FCSTD DOCUMENT  (FreeCAD 1.0R39109 (Git))
Label: asm_cam_holder
License: All rights reserved
LicenseURL: https://en.wikipedia.org/wiki/All_rights_reserved
objects: App::Link×24, App::FeaturePython×5, Assembly::AssemblyLink×4, Assembly::JointGroup×1, Assembly::AssemblyObject×1
EXTERNAL_REF file=../parts/cam_holder/cam_holder_plate.FCStd obj=Body
EXTERNAL_REF file=asm_shf.FCStd obj=Assembly
EXTERNAL_REF file=asm_shf.FCStd obj=SHF12
EXTERNAL_REF file=asm_shf.FCStd obj=Hex_socket_head_cap_screw_DIN_912_M4_15_0
EXTERNAL_REF file=asm_shf.FCStd obj=Hex_socket_head_cap_screw_DIN_912_M5_15_0
EXTERNAL_REF file=asm_shf.FCStd obj=Hex_socket_head_cap_screw_DIN_912_M5_15_001
EXTERNAL_REF file=asm_rpi.FCStd obj=Assembly
EXTERNAL_REF file=asm_rpi.FCStd obj=Raspberry_Pi_4_Model_B
EXTERNAL_REF file=asm_rpi.FCStd obj=Hex_screw_M2_5_04_0
EXTERNAL_REF file=asm_rpi.FCStd obj=Hex_screw_M2_5_04_001
EXTERNAL_REF file=asm_rpi.FCStd obj=Hex_screw_M2_5_04_002
EXTERNAL_REF file=asm_rpi.FCStd obj=Hex_screw_M2_5_04_003
EXTERNAL_REF file=asm_cam_mount.FCStd obj=Assembly
EXTERNAL_REF file=asm_cam_mount.FCStd obj=cam_holder_base
EXTERNAL_REF file=asm_cam_mount.FCStd obj=Raspberry_Pi_HQ_Camera_with_cs_mount_lens_v014
EXTERNAL_REF file=asm_cam_mount.FCStd obj=Hex_screw_M2_5_04_0
EXTERNAL_REF file=asm_cam_mount.FCStd obj=Hex_screw_M2_5_04_001
EXTERNAL_REF file=asm_cam_mount.FCStd obj=Hex_screw_M2_5_04_002
EXTERNAL_REF file=asm_cam_mount.FCStd obj=Hex_screw_M2_5_04_003
EXTERNAL_REF file=asm_cam_mount.FCStd obj=Hex_screw_M4_10_0
EXTERNAL_REF file=asm_cam_mount.FCStd obj=Hex_screw_M4_10_001
EXTERNAL_REF file=asm_cam_mount.FCStd obj=Hex_screw_M4_10_002
EXTERNAL_REF file=asm_cam_mount.FCStd obj=Hex_screw_M4_10_003

FEATURE [App::Link] cam_holder_plate
  LinkedObject = -> <external ../parts/cam_holder/cam_holder_plate.FCStd>#Body
FEATURE [App::FeaturePython] GroundedJoint  # Assembly grounded joint (typed FeaturePython)
  ObjectToGround = -> cam_holder_plate
FEATURE [App::Link] SHF12
  LinkedObject = -> <external asm_shf.FCStd>#SHF12
FEATURE [App::Link] Hex_socket_head_cap_screw_DIN_912_M4_15_0  label="Hex socket head cap screw DIN 912 M4 15.0"
  LinkPlacement = pos=(12.25,6.5,11.5) rot=(0,-1,0;1.5708rad)
  LinkedObject = -> <external asm_shf.FCStd>#Hex_socket_head_cap_screw_DIN_912_M4_15_0
  Placement = pos=(12.25,6.5,11.5) rot=(0,-1,0;1.5708rad)
FEATURE [App::Link] Hex_socket_head_cap_screw_DIN_912_M5_15_0  label="Hex socket head cap screw DIN 912 M5 15.0"
  LinkPlacement = pos=(18,11,1.16e-14) rot=(0.57735,-0.57735,0.57735;2.0944rad)
  LinkedObject = -> <external asm_shf.FCStd>#Hex_socket_head_cap_screw_DIN_912_M5_15_0
  Placement = pos=(18,11,1.16e-14) rot=(0.57735,-0.57735,0.57735;2.0944rad)
FEATURE [App::Link] Hex_socket_head_cap_screw_DIN_912_M5_15_001  label="Hex socket head cap screw DIN 912 M5 15.001"
  LinkPlacement = pos=(-18,11,1.16e-14) rot=(0.57735,-0.57735,0.57735;2.0944rad)
  LinkedObject = -> <external asm_shf.FCStd>#Hex_socket_head_cap_screw_DIN_912_M5_15_001
  Placement = pos=(-18,11,1.16e-14) rot=(0.57735,-0.57735,0.57735;2.0944rad)
FEATURE [Assembly::AssemblyLink] asm_SHF
  Group = -> [SHF12,Hex_socket_head_cap_screw_DIN_912_M4_15_0,Hex_socket_head_cap_screw_DIN_912_M5_15_0,Hex_socket_head_cap_screw_DIN_912_M5_15_001]
  LinkedObject = -> <external asm_shf.FCStd>#Assembly
  Origin = -> Origin001
  Placement = pos=(0,38,3) rot=(0,0.707107,0.707107;3.14159rad)
  Rigid = true
FEATURE [App::Link] SHF013
  LinkedObject = -> <external asm_shf.FCStd>#SHF12
FEATURE [App::Link] Hex_socket_head_cap_screw_DIN_912_M4_15_001  label="Hex socket head cap screw DIN 912 M4 15.001"
  LinkPlacement = pos=(12.25,6.5,11.5) rot=(0,-1,0;1.5708rad)
  LinkedObject = -> <external asm_shf.FCStd>#Hex_socket_head_cap_screw_DIN_912_M4_15_0
  Placement = pos=(12.25,6.5,11.5) rot=(0,-1,0;1.5708rad)
FEATURE [App::Link] Hex_socket_head_cap_screw_DIN_912_M5_15_002  label="Hex socket head cap screw DIN 912 M5 15.002"
  LinkPlacement = pos=(18,11,1.16e-14) rot=(0.57735,-0.57735,0.57735;2.0944rad)
  LinkedObject = -> <external asm_shf.FCStd>#Hex_socket_head_cap_screw_DIN_912_M5_15_0
  Placement = pos=(18,11,1.16e-14) rot=(0.57735,-0.57735,0.57735;2.0944rad)
FEATURE [App::Link] Hex_socket_head_cap_screw_DIN_912_M5_15_003  label="Hex socket head cap screw DIN 912 M5 15.003"
  LinkPlacement = pos=(-18,11,1.16e-14) rot=(0.57735,-0.57735,0.57735;2.0944rad)
  LinkedObject = -> <external asm_shf.FCStd>#Hex_socket_head_cap_screw_DIN_912_M5_15_001
  Placement = pos=(-18,11,1.16e-14) rot=(0.57735,-0.57735,0.57735;2.0944rad)
FEATURE [Assembly::AssemblyLink] asm_SHF001
  Group = -> [SHF013,Hex_socket_head_cap_screw_DIN_912_M4_15_001,Hex_socket_head_cap_screw_DIN_912_M5_15_002,Hex_socket_head_cap_screw_DIN_912_M5_15_003]
  LinkedObject = -> <external asm_shf.FCStd>#Assembly
  Origin = -> Origin002
  Placement = pos=(0,-38,3) rot=(1,0,0;1.5708rad)
  Rigid = true
FEATURE [App::Link] Raspberry_Pi_4_Model_B  label="Raspberry Pi 4 Model B"
  LinkPlacement = pos=(0,8.25,-5.85) rot=(1,0,0;1.5708rad)
  LinkedObject = -> <external asm_rpi.FCStd>#Raspberry_Pi_4_Model_B
  Placement = pos=(0,8.25,-5.85) rot=(1,0,0;1.5708rad)
FEATURE [App::Link] Hex_screw_M2_5_04_0  label="Hex screw M2.5 04.0"
  LinkPlacement = pos=(54.5575,25.7632,-2.56) rot=(-0.707107,0.707107,0;3.14159rad)
  LinkedObject = -> <external asm_rpi.FCStd>#Hex_screw_M2_5_04_0
  Placement = pos=(54.5575,25.7632,-2.56) rot=(-0.707107,0.707107,0;3.14159rad)
FEATURE [App::Link] Hex_screw_M2_5_04_001  label="Hex screw M2.5 04.001"
  LinkPlacement = pos=(-3.44249,-23.2368,-2.56001) rot=(-0.707107,0.707107,0;3.14159rad)
  LinkedObject = -> <external asm_rpi.FCStd>#Hex_screw_M2_5_04_001
  Placement = pos=(-3.44249,-23.2368,-2.56001) rot=(-0.707107,0.707107,0;3.14159rad)
FEATURE [App::Link] Hex_screw_M2_5_04_002  label="Hex screw M2.5 04.002"
  LinkPlacement = pos=(-3.44249,25.7632,-2.56) rot=(-0.707107,0.707107,0;3.14159rad)
  LinkedObject = -> <external asm_rpi.FCStd>#Hex_screw_M2_5_04_002
  Placement = pos=(-3.44249,25.7632,-2.56) rot=(-0.707107,0.707107,0;3.14159rad)
FEATURE [App::Link] Hex_screw_M2_5_04_003  label="Hex screw M2.5 04.003"
  LinkPlacement = pos=(54.5575,-23.2368,-2.56001) rot=(-0.707107,0.707107,0;3.14159rad)
  LinkedObject = -> <external asm_rpi.FCStd>#Hex_screw_M2_5_04_003
  Placement = pos=(54.5575,-23.2368,-2.56001) rot=(-0.707107,0.707107,0;3.14159rad)
FEATURE [Assembly::AssemblyLink] asm_rpi
  Group = -> [Raspberry_Pi_4_Model_B,Hex_screw_M2_5_04_0,Hex_screw_M2_5_04_001,Hex_screw_M2_5_04_002,Hex_screw_M2_5_04_003]
  LinkedObject = -> <external asm_rpi.FCStd>#Assembly
  Origin = -> Origin003
  Placement = pos=(-63.8,10.25,9.64) rot=(0,0,1;3.14159rad)
  Rigid = true
FEATURE [App::Link] cam_holder_base
  LinkPlacement = pos=(0,0,0) rot=(1,0,0;3.14159rad)
  LinkedObject = -> <external asm_cam_mount.FCStd>#cam_holder_base
  Placement = pos=(0,0,0) rot=(1,0,0;3.14159rad)
FEATURE [App::Link] Raspberry_Pi_HQ_Camera_with_cs_mount_lens_v014  label="Raspberry Pi HQ Camera with cs mount lens v014"
  LinkPlacement = pos=(-18.96,19,-3.8) rot=(1,0,0;1.5708rad)
  LinkedObject = -> <external asm_cam_mount.FCStd>#Raspberry_Pi_HQ_Camera_with_cs_mount_lens_v014
  Placement = pos=(-18.96,19,-3.8) rot=(1,0,0;1.5708rad)
FEATURE [App::Link] Hex_screw_M2_5_04_004  label="Hex screw M2.5 04.004"
  LinkPlacement = pos=(-7.97317,-20.5575,-6.3) rot=(0,0,1;0rad)
  LinkedObject = -> <external asm_cam_mount.FCStd>#Hex_screw_M2_5_04_0
  Placement = pos=(-7.97317,-20.5575,-6.3) rot=(0,0,1;0rad)
FEATURE [App::Link] Hex_screw_M2_5_04_005  label="Hex screw M2.5 04.005"
  LinkPlacement = pos=(22.0268,-20.5575,-6.3) rot=(0,0,1;0rad)
  LinkedObject = -> <external asm_cam_mount.FCStd>#Hex_screw_M2_5_04_001
  Placement = pos=(22.0268,-20.5575,-6.3) rot=(0,0,1;0rad)
FEATURE [App::Link] Hex_screw_M2_5_04_006  label="Hex screw M2.5 04.006"
  LinkPlacement = pos=(22.0268,-50.5575,-6.3) rot=(0,0,1;0rad)
  LinkedObject = -> <external asm_cam_mount.FCStd>#Hex_screw_M2_5_04_002
  Placement = pos=(22.0268,-50.5575,-6.3) rot=(0,0,1;0rad)
FEATURE [App::Link] Hex_screw_M2_5_04_007  label="Hex screw M2.5 04.007"
  LinkPlacement = pos=(-7.97317,-50.5575,-6.3) rot=(0,0,1;0rad)
  LinkedObject = -> <external asm_cam_mount.FCStd>#Hex_screw_M2_5_04_003
  Placement = pos=(-7.97317,-50.5575,-6.3) rot=(0,0,1;0rad)
FEATURE [App::Link] Hex_screw_M4_10_0  label="Hex screw M4 10.0"
  LinkPlacement = pos=(-25.9732,-58.0575,-20.5) rot=(0,0,1;0rad)
  LinkedObject = -> <external asm_cam_mount.FCStd>#Hex_screw_M4_10_0
  Placement = pos=(-25.9732,-58.0575,-20.5) rot=(0,0,1;0rad)
FEATURE [App::Link] Hex_screw_M4_10_001  label="Hex screw M4 10.001"
  LinkPlacement = pos=(-25.9732,-20.0575,-20.5) rot=(0,0,1;0rad)
  LinkedObject = -> <external asm_cam_mount.FCStd>#Hex_screw_M4_10_001
  Placement = pos=(-25.9732,-20.0575,-20.5) rot=(0,0,1;0rad)
FEATURE [App::Link] Hex_screw_M4_10_002  label="Hex screw M4 10.002"
  LinkPlacement = pos=(39.9468,-58.0575,-20.5) rot=(0,0,1;0rad)
  LinkedObject = -> <external asm_cam_mount.FCStd>#Hex_screw_M4_10_002
  Placement = pos=(39.9468,-58.0575,-20.5) rot=(0,0,1;0rad)
FEATURE [App::Link] Hex_screw_M4_10_003  label="Hex screw M4 10.003"
  LinkPlacement = pos=(39.9468,-20.0575,-20.5) rot=(0,0,1;0rad)
  LinkedObject = -> <external asm_cam_mount.FCStd>#Hex_screw_M4_10_003
  Placement = pos=(39.9468,-20.0575,-20.5) rot=(0,0,1;0rad)
FEATURE [Assembly::AssemblyLink] asm_cam_mount
  Group = -> [cam_holder_base,Raspberry_Pi_HQ_Camera_with_cs_mount_lens_v014,Hex_screw_M2_5_04_004,Hex_screw_M2_5_04_005,Hex_screw_M2_5_04_006,Hex_screw_M2_5_04_007,Hex_screw_M4_10_0,Hex_screw_M4_10_001,Hex_screw_M4_10_002,Hex_screw_M4_10_003]
  LinkedObject = -> <external asm_cam_mount.FCStd>#Assembly
  Origin = -> Origin004
  Placement = pos=(58.5311,-2.9e-15,15.5) rot=(0,0,1;4.71239rad)
  Rigid = true
FEATURE [App::FeaturePython] Joint  label="Fixed"  # Assembly joint (typed FeaturePython)
  Activated = true
  AngleMax = 0
  AngleMin = 0
  Detach1 = false
  Detach2 = false
  Distance = 0
  Distance2 = 0
  EnableAngleMax = false
  EnableAngleMin = false
  EnableLengthMax = false
  EnableLengthMin = false
  JointType = 0 (Fixed)
  LengthMax = 0
  LengthMin = 0
  Offset2 = pos=(0,0,0) rot=(0,0,1;1.5708rad)
  Placement1 = pos=(19,-0.79,24.5) rot=(0.57735,0.57735,0.57735;4.18879rad)
  Placement2 = pos=(-82.8,26.5,3) rot=(0,0,1;1.5708rad)
  Reference1 = -> Assembly [asm_rpi.Raspberry_Pi_4_Model_B.Part__Feature.Edge337,asm_rpi.Raspberry_Pi_4_Model_B.Part__Feature.Edge337]
  Reference2 = -> Assembly [cam_holder_plate.Edge66,cam_holder_plate.Edge66]
FEATURE [App::FeaturePython] Joint001  label="Fixed001"  # Assembly joint (typed FeaturePython)
  Activated = true
  AngleMax = 0
  AngleMin = 0
  Detach1 = false
  Detach2 = false
  Distance = 0
  Distance2 = 0
  EnableAngleMax = false
  EnableAngleMin = false
  EnableLengthMax = false
  EnableLengthMin = false
  JointType = 0 (Fixed)
  LengthMax = 0
  LengthMin = 0
  Offset2 = pos=(0,0,0) rot=(0,0,-1;1.5708rad)
  Placement1 = pos=(18,0,1.16e-14) rot=(-0.57735,0.57735,0.57735;2.0944rad)
  Placement2 = pos=(-18,38,3) rot=(0,0,-1;1.5708rad)
  Reference1 = -> Assembly [asm_SHF.SHF12.Edge109,asm_SHF.SHF12.Edge109]
  Reference2 = -> Assembly [cam_holder_plate.Edge45,cam_holder_plate.Edge45]
FEATURE [App::FeaturePython] Joint002  label="Fixed002"  # Assembly joint (typed FeaturePython)
  Activated = true
  AngleMax = 0
  AngleMin = 0
  Detach1 = false
  Detach2 = false
  Distance = 0
  Distance2 = 0
  EnableAngleMax = false
  EnableAngleMin = false
  EnableLengthMax = false
  EnableLengthMin = false
  JointType = 0 (Fixed)
  LengthMax = 0
  LengthMin = 0
  Offset2 = pos=(0,0,0) rot=(0,0,-1;1.5708rad)
  Placement1 = pos=(-18,0,1.16e-14) rot=(0.57735,0.57735,0.57735;4.18879rad)
  Placement2 = pos=(-18,-38,3) rot=(0,0,-1;1.5708rad)
  Reference1 = -> Assembly [asm_SHF001.SHF013.Edge27,asm_SHF001.SHF013.Edge27]
  Reference2 = -> Assembly [cam_holder_plate.Edge51,cam_holder_plate.Edge51]
FEATURE [App::FeaturePython] Joint003  label="Fixed003"  # Assembly joint (typed FeaturePython)
  Activated = true
  AngleMax = 0
  AngleMin = 0
  Detach1 = false
  Detach2 = false
  Distance = 0
  Distance2 = 0
  EnableAngleMax = false
  EnableAngleMin = false
  EnableLengthMax = false
  EnableLengthMin = false
  JointType = 0 (Fixed)
  LengthMax = 0
  LengthMin = 0
  Offset2 = pos=(0,0,0) rot=(0,0,-1;1.5708rad)
  Placement1 = pos=(32.96,22.5,12.5) rot=(0,0,1;0rad)
  Placement2 = pos=(36.0311,-32.96,3) rot=(0,0,-1;1.5708rad)
  Reference1 = -> Assembly [asm_cam_mount.cam_holder_base.Edge111,asm_cam_mount.cam_holder_base.Edge111]
  Reference2 = -> Assembly [cam_holder_plate.Edge39,cam_holder_plate.Edge39]
FEATURE [Assembly::JointGroup] Joints
  Group = -> [GroundedJoint,Joint,Joint001,Joint002,Joint003]
FEATURE [Assembly::AssemblyObject] Assembly  label="asm_cam_holder"
  Group = -> [Joints,cam_holder_plate,GroundedJoint,asm_SHF,asm_SHF001,asm_rpi,asm_cam_mount,Joint,Joint001,Joint002,Joint003]
  Origin = -> Origin
  Type = Assembly

RESOLVED EXTERNAL PARTS (link-assembly join: the EXTERNAL_REF files above that resolve inside this repo's crawl, each included once):
---- part ../parts/cam_holder/cam_holder_plate.FCStd = doc fcstd_973b0cef81d6 ----
FCSTD DOCUMENT  (FreeCAD 1.0R39109 (Git))
Label: cam_holder_plate
License: All rights reserved
LicenseURL: https://en.wikipedia.org/wiki/All_rights_reserved
objects: Sketcher::SketchObject×2, PartDesign::Pad×2, PartDesign::Body×1
note: 11 computed .brp shape members not serialized (recipe doc carries the construction recipe); baked Part::Feature solids carry a one-line shape summary decoded from their .brp

FEATURE [Sketcher::SketchObject] Sketch
  ArcFitTolerance = 1e-06
  AttachmentSupport = -> [XY_Plane]
  FullyConstrained = false
  MakeInternals = false
  MapMode = 5
  sketch-geometry (25):
    g0: LineSegment StartX=-110 StartY=50 StartZ=0 EndX=-110 EndY=-50 EndZ=0
    g1: LineSegment StartX=-110 StartY=-50 StartZ=0 EndX=110 EndY=-50 EndZ=0
    g2: LineSegment StartX=110 StartY=-50 StartZ=0 EndX=110 EndY=50 EndZ=0
    g3: LineSegment StartX=110 StartY=50 StartZ=0 EndX=-110 EndY=50 EndZ=0
    g4: GeomPoint [constr] X=0 Y=0 Z=0
    g5: Circle CenterX=-82.8 CenterY=26.5 CenterZ=0 NormalX=0 NormalY=0 NormalZ=1 AngleXU=0 Radius=1.35
    g6: Circle CenterX=-82.8 CenterY=-22.5 CenterZ=0 NormalX=0 NormalY=0 NormalZ=1 AngleXU=0 Radius=1.35
    g7: Circle CenterX=-24.8 CenterY=-22.5 CenterZ=0 NormalX=0 NormalY=0 NormalZ=1 AngleXU=0 Radius=1.35
    g8: Circle CenterX=-24.8 CenterY=26.5 CenterZ=0 NormalX=0 NormalY=0 NormalZ=1 AngleXU=0 Radius=1.35
    g9: Circle CenterX=36.0311 CenterY=32.96 CenterZ=0 NormalX=0 NormalY=0 NormalZ=1 AngleXU=0 Radius=1.95
    g10: Circle CenterX=36.0311 CenterY=-32.96 CenterZ=0 NormalX=0 NormalY=0 NormalZ=1 AngleXU=0 Radius=1.95
    g11: Circle CenterX=74.0311 CenterY=32.96 CenterZ=0 NormalX=0 NormalY=0 NormalZ=1 AngleXU=0 Radius=1.95
    g12: Circle CenterX=74.0311 CenterY=-32.96 CenterZ=0 NormalX=0 NormalY=0 NormalZ=1 AngleXU=0 Radius=1.95
    g13: Circle CenterX=-104 CenterY=-44 CenterZ=0 NormalX=0 NormalY=0 NormalZ=1 AngleXU=0 Radius=2.5
    g14: Circle CenterX=-104 CenterY=44 CenterZ=0 NormalX=0 NormalY=0 NormalZ=1 AngleXU=0 Radius=2.5
    g15: Circle CenterX=104 CenterY=44 CenterZ=0 NormalX=0 NormalY=0 NormalZ=1 AngleXU=0 Radius=2.5
    g16: Circle CenterX=104 CenterY=-44 CenterZ=0 NormalX=0 NormalY=0 NormalZ=1 AngleXU=0 Radius=2.5
    g17: Circle CenterX=0 CenterY=-38 CenterZ=0 NormalX=0 NormalY=0 NormalZ=1 AngleXU=0 Radius=6.5
    g18: Circle CenterX=18 CenterY=-38 CenterZ=0 NormalX=0 NormalY=0 NormalZ=1 AngleXU=0 Radius=1.95
    g19: Circle CenterX=-18 CenterY=-38 CenterZ=0 NormalX=0 NormalY=0 NormalZ=1 AngleXU=0 Radius=1.95
    g20: Circle CenterX=0 CenterY=38 CenterZ=0 NormalX=0 NormalY=0 NormalZ=1 AngleXU=0 Radius=6.5
    g21: Circle CenterX=18 CenterY=38 CenterZ=0 NormalX=0 NormalY=0 NormalZ=1 AngleXU=0 Radius=1.95
    g22: Circle CenterX=-18 CenterY=38 CenterZ=0 NormalX=0 NormalY=0 NormalZ=1 AngleXU=0 Radius=1.95
    g23: LineSegment [constr] StartX=-104 StartY=42.1544 StartZ=0 EndX=-104 EndY=53.0988 EndZ=0
    g24: LineSegment [constr] StartX=-108.248 StartY=44 StartZ=0 EndX=-95.3558 EndY=44 EndZ=0
  constraints (66):
    c: Coincident(g0,g1)
    c: Coincident(g1,g2)
    c: Coincident(g2,g3)
    c: Coincident(g3,g0)
    c: Vertical(g0)
    c: Vertical(g2)
    c: Horizontal(g1)
    c: Horizontal(g3)
    c: Symmetric(g2,g0,g4)
    c: Coincident(g4,g-1)
    c: DistanceX(g5,g8) = 58
    c: Horizontal(g8,g5)
    c: DistanceY(g6,g5) = 49
    c: Diameter(g5) = 2.7
    c: Equal(g5,g6)
    c: Equal(g6,g7)
    c: Equal(g7,g8)
    c: Horizontal(g9,g11)
    c: Horizontal(g10,g12)
    c: Vertical(g9,g10)
    c: Vertical(g11,g12)
    c: Equal(g9,g11)
    c: Equal(g11,g10)
    c: Equal(g10,g12)
    c: Diameter(g9) = 3.9
    c: DistanceX(g9,g11) = 38
    c: DistanceY(g10,g9) = 65.92
    c: Distance(g0,g0) = 100
    c: DistanceX(g3,g3) = 220
    c: Horizontal(g16,g13)
    c: Vertical(g16,g15)
    c: Equal(g14,g13)
    c: Equal(g15,g14)
    c: Equal(g16,g15)
    c: Diameter(g14) = 5
    c: DistanceY(g14,g0) = 6
    c: DistanceX(g0,g14) = 6
    c: Symmetric(g14,g15,g-2)
    c: Symmetric(g13,g14,g-1)
    c: Horizontal(g6,g7)
    c: Vertical(g5,g6)
    c: PointOnObject(g17,g-2)
    c: Horizontal(g19,g17)
    c: Horizontal(g17,g18)
    c: DistanceX(g19,g17) = 18
    c: DistanceX(g17,g18) = 18
    c: Diameter(g19) = 3.9
    c: Diameter(g17) = 13
    c: Vertical(g7,g8)
    c: Horizontal(g20,g22)
    c: Horizontal(g22,g21)
    c: Equal(g21,g18)
    c: Equal(g20,g17)
    c: Distance(g17,g1) = 12
    c: Equal(g18,g19)
    c: Symmetric(g17,g20,g-1)
    c: Equal(g22,g19)
    c: Vertical(g19,g22)
    c: Vertical(g21,g18)
    c: PointOnObject(g14,g23)
    c: Vertical(g23)
    c: Horizontal(g24)
    c: PointOnObject(g14,g24)
    c: Distance(g5,g23) = 21.2
    c: Distance(g5,g24) = 17.5
    c: Distance(g9,g-1) = 32.96
FEATURE [PartDesign::Pad] Pad
  Direction = (0,0,1)
  Length = 3
  Length2 = 10
  Profile = -> Sketch
  ReferenceAxis = -> Sketch [N_Axis]
  Refine = true
  Suppressed = false
  Type = 0
FEATURE [Sketcher::SketchObject] Sketch002
  ArcFitTolerance = 1e-06
  FullyConstrained = true
  MakeInternals = false
  MapMode = 5
  Placement = pos=(0,0,5) rot=(0,0,1;0rad)
  sketch-geometry (8):
    g0: Circle CenterX=-82.8 CenterY=26.5 CenterZ=0 NormalX=0 NormalY=0 NormalZ=1 AngleXU=0 Radius=1.35
    g1: Circle CenterX=-24.8 CenterY=26.5 CenterZ=0 NormalX=0 NormalY=0 NormalZ=1 AngleXU=0 Radius=1.35
    g2: Circle CenterX=-24.8 CenterY=-22.5 CenterZ=0 NormalX=0 NormalY=0 NormalZ=1 AngleXU=0 Radius=1.35
    g3: Circle CenterX=-82.8 CenterY=-22.5 CenterZ=0 NormalX=0 NormalY=0 NormalZ=1 AngleXU=0 Radius=1.35
    g4: Circle CenterX=-82.8 CenterY=26.5 CenterZ=0 NormalX=0 NormalY=0 NormalZ=1 AngleXU=0 Radius=3.85
    g5: Circle CenterX=-24.8 CenterY=26.5 CenterZ=0 NormalX=0 NormalY=0 NormalZ=1 AngleXU=0 Radius=3.85
    g6: Circle CenterX=-24.8 CenterY=-22.5 CenterZ=0 NormalX=0 NormalY=0 NormalZ=1 AngleXU=0 Radius=3.85
    g7: Circle CenterX=-82.8 CenterY=-22.5 CenterZ=0 NormalX=0 NormalY=0 NormalZ=1 AngleXU=0 Radius=3.85
  constraints (16):
    c: Coincident(g0,g-3)
    c: Equal(g0,g-3)
    c: Coincident(g1,g-5)
    c: Equal(g1,g-5)
    c: Coincident(g2,g-6)
    c: Equal(g2,g-6)
    c: Coincident(g3,g-7)
    c: Equal(g3,g-7)
    c: Coincident(g4,g0)
    c: Distance(g0,g4) = 2.5
    c: Coincident(g5,g1)
    c: Coincident(g6,g2)
    c: Coincident(g7,g3)
    c: Equal(g4,g7)
    c: Equal(g7,g6)
    c: Equal(g6,g5)
FEATURE [PartDesign::Pad] Pad001
  BaseFeature = -> Pad
  Direction = (0,0,1)
  Length = 5
  Length2 = 10
  Profile = -> Sketch002
  ReferenceAxis = -> Sketch002 [N_Axis]
  Refine = true
  Suppressed = false
  Type = 0
FEATURE [PartDesign::Body] Body  label="cam_holder_plate"
  AllowCompound = false
  Group = -> [Sketch,Pad,Sketch002,Pad001]
  Origin = -> Origin
  Tip = -> Pad001
---- part asm_cam_mount.FCStd = doc fcstd_c71f351d43c1 ----
FCSTD DOCUMENT  (FreeCAD 1.0R39109 (Git))
Label: asm_cam_mount
License: All rights reserved
LicenseURL: https://en.wikipedia.org/wiki/All_rights_reserved
objects: App::Link×10, App::FeaturePython×10, Assembly::JointGroup×1, Assembly::AssemblyObject×1
EXTERNAL_REF file=../parts/cam_holder/cam_holder_base.FCStd obj=Body
EXTERNAL_REF file=../downloads/raspberry_pi_camera.FCStd obj=Raspberry_Pi_HQ_Camera_with_cs_mount_lens_v3
EXTERNAL_REF file=../secondary/bolts.FCStd obj=Body003
EXTERNAL_REF file=../secondary/bolts.FCStd obj=Body002

FEATURE [App::Link] cam_holder_base
  LinkPlacement = pos=(0,0,0) rot=(1,0,0;3.14159rad)
  LinkedObject = -> <external ../parts/cam_holder/cam_holder_base.FCStd>#Body
  Placement = pos=(0,0,0) rot=(1,0,0;3.14159rad)
FEATURE [App::FeaturePython] GroundedJoint  # Assembly grounded joint (typed FeaturePython)
  ObjectToGround = -> cam_holder_base
  Placement = pos=(0,0,0) rot=(1,0,0;3.14159rad)
FEATURE [App::Link] Raspberry_Pi_HQ_Camera_with_cs_mount_lens_v014  label="Raspberry Pi HQ Camera with cs mount lens v014"
  LinkPlacement = pos=(-18.96,19,-3.8) rot=(1,0,0;1.5708rad)
  LinkedObject = -> <external ../downloads/raspberry_pi_camera.FCStd>#Raspberry_Pi_HQ_Camera_with_cs_mount_lens_v3
  Placement = pos=(-18.96,19,-3.8) rot=(1,0,0;1.5708rad)
FEATURE [App::FeaturePython] Joint  label="Fixed"  # Assembly joint (typed FeaturePython)
  Activated = true
  AngleMax = 0
  AngleMin = 0
  Detach1 = false
  Detach2 = false
  Distance = 0
  Distance2 = 0
  EnableAngleMax = false
  EnableAngleMin = false
  EnableLengthMax = false
  EnableLengthMin = false
  JointType = 0 (Fixed)
  LengthMax = 0
  LengthMin = 0
  Placement1 = pos=(-14.96,-15,2.5) rot=(0,0,1;0rad)
  Placement2 = pos=(4,1.3,4) rot=(-1,0,0;1.5708rad)
  Reference1 = -> Assembly [cam_holder_base.Edge44,cam_holder_base.Edge44]
  Reference2 = -> Assembly [Raspberry_Pi_HQ_Camera_with_cs_mount_lens_v014.Part__Feature.Edge16,Raspberry_Pi_HQ_Camera_with_cs_mount_lens_v014.Part__Feature.Edge16]
FEATURE [App::Link] Hex_screw_M2_5_04_0  label="Hex screw M2.5 04.0"
  LinkPlacement = pos=(-7.97317,-20.5575,-6.3) rot=(0,0,1;0rad)
  LinkedObject = -> <external ../secondary/bolts.FCStd>#Body003
  Placement = pos=(-7.97317,-20.5575,-6.3) rot=(0,0,1;0rad)
FEATURE [App::Link] Hex_screw_M2_5_04_001  label="Hex screw M2.5 04.001"
  LinkPlacement = pos=(22.0268,-20.5575,-6.3) rot=(0,0,1;0rad)
  LinkedObject = -> <external ../secondary/bolts.FCStd>#Body003
  Placement = pos=(22.0268,-20.5575,-6.3) rot=(0,0,1;0rad)
FEATURE [App::Link] Hex_screw_M2_5_04_002  label="Hex screw M2.5 04.002"
  LinkPlacement = pos=(22.0268,-50.5575,-6.3) rot=(0,0,1;0rad)
  LinkedObject = -> <external ../secondary/bolts.FCStd>#Body003
  Placement = pos=(22.0268,-50.5575,-6.3) rot=(0,0,1;0rad)
FEATURE [App::Link] Hex_screw_M2_5_04_003  label="Hex screw M2.5 04.003"
  LinkPlacement = pos=(-7.97317,-50.5575,-6.3) rot=(0,0,1;0rad)
  LinkedObject = -> <external ../secondary/bolts.FCStd>#Body003
  Placement = pos=(-7.97317,-50.5575,-6.3) rot=(0,0,1;0rad)
FEATURE [App::FeaturePython] Joint001  label="Fixed001"  # Assembly joint (typed FeaturePython)
  Activated = true
  AngleMax = 0
  AngleMin = 0
  Detach1 = false
  Detach2 = false
  Distance = 0
  Distance2 = 0
  EnableAngleMax = false
  EnableAngleMin = false
  EnableLengthMax = false
  EnableLengthMin = false
  JointType = 0 (Fixed)
  LengthMax = 0
  LengthMin = 0
  Placement1 = pos=(-6.98683,35.5575,2.5) rot=(0,0,1;0rad)
  Placement2 = pos=(4,0,4) rot=(1,0,0;1.5708rad)
  Reference1 = -> Assembly [Hex_screw_M2_5_04_0.Edge4,Hex_screw_M2_5_04_0.Edge4]
  Reference2 = -> Assembly [Raspberry_Pi_HQ_Camera_with_cs_mount_lens_v014.Part__Feature.Edge18,Raspberry_Pi_HQ_Camera_with_cs_mount_lens_v014.Part__Feature.Edge18]
FEATURE [App::FeaturePython] Joint002  label="Fixed002"  # Assembly joint (typed FeaturePython)
  Activated = true
  AngleMax = 0
  AngleMin = 0
  Detach1 = false
  Detach2 = false
  Distance = 0
  Distance2 = 0
  EnableAngleMax = false
  EnableAngleMin = false
  EnableLengthMax = false
  EnableLengthMin = false
  JointType = 0 (Fixed)
  LengthMax = 0
  LengthMin = 0
  Placement1 = pos=(-6.98683,35.5575,2.5) rot=(0,0,1;0rad)
  Placement2 = pos=(34,0,4) rot=(1,0,0;1.5708rad)
  Reference1 = -> Assembly [Hex_screw_M2_5_04_001.Edge4,Hex_screw_M2_5_04_001.Edge4]
  Reference2 = -> Assembly [Raspberry_Pi_HQ_Camera_with_cs_mount_lens_v014.Part__Feature.Edge24,Raspberry_Pi_HQ_Camera_with_cs_mount_lens_v014.Part__Feature.Edge24]
FEATURE [App::FeaturePython] Joint003  label="Fixed003"  # Assembly joint (typed FeaturePython)
  Activated = true
  AngleMax = 0
  AngleMin = 0
  Detach1 = false
  Detach2 = false
  Distance = 0
  Distance2 = 0
  EnableAngleMax = false
  EnableAngleMin = false
  EnableLengthMax = false
  EnableLengthMin = false
  JointType = 0 (Fixed)
  LengthMax = 0
  LengthMin = 0
  Placement1 = pos=(-6.98683,35.5575,2.5) rot=(0,0,1;0rad)
  Placement2 = pos=(34,0,34) rot=(1,0,0;1.5708rad)
  Reference1 = -> Assembly [Hex_screw_M2_5_04_002.Edge4,Hex_screw_M2_5_04_002.Edge4]
  Reference2 = -> Assembly [Raspberry_Pi_HQ_Camera_with_cs_mount_lens_v014.Part__Feature.Edge22,Raspberry_Pi_HQ_Camera_with_cs_mount_lens_v014.Part__Feature.Edge22]
FEATURE [App::FeaturePython] Joint004  label="Fixed004"  # Assembly joint (typed FeaturePython)
  Activated = true
  AngleMax = 0
  AngleMin = 0
  Detach1 = false
  Detach2 = false
  Distance = 0
  Distance2 = 0
  EnableAngleMax = false
  EnableAngleMin = false
  EnableLengthMax = false
  EnableLengthMin = false
  JointType = 0 (Fixed)
  LengthMax = 0
  LengthMin = 0
  Placement1 = pos=(-6.98683,35.5575,2.5) rot=(0,0,1;0rad)
  Placement2 = pos=(4,0,34) rot=(1,0,0;1.5708rad)
  Reference1 = -> Assembly [Hex_screw_M2_5_04_003.Edge4,Hex_screw_M2_5_04_003.Edge4]
  Reference2 = -> Assembly [Raspberry_Pi_HQ_Camera_with_cs_mount_lens_v014.Part__Feature.Edge20,Raspberry_Pi_HQ_Camera_with_cs_mount_lens_v014.Part__Feature.Edge20]
FEATURE [App::Link] Hex_screw_M4_10_0  label="Hex screw M4 10.0"
  LinkPlacement = pos=(-25.9732,-58.0575,-20.5) rot=(0,0,1;0rad)
  LinkedObject = -> <external ../secondary/bolts.FCStd>#Body002
  Placement = pos=(-25.9732,-58.0575,-20.5) rot=(0,0,1;0rad)
FEATURE [App::Link] Hex_screw_M4_10_001  label="Hex screw M4 10.001"
  LinkPlacement = pos=(-25.9732,-20.0575,-20.5) rot=(0,0,1;0rad)
  LinkedObject = -> <external ../secondary/bolts.FCStd>#Body002
  Placement = pos=(-25.9732,-20.0575,-20.5) rot=(0,0,1;0rad)
FEATURE [App::Link] Hex_screw_M4_10_002  label="Hex screw M4 10.002"
  LinkPlacement = pos=(39.9468,-58.0575,-20.5) rot=(0,0,1;0rad)
  LinkedObject = -> <external ../secondary/bolts.FCStd>#Body002
  Placement = pos=(39.9468,-58.0575,-20.5) rot=(0,0,1;0rad)
FEATURE [App::Link] Hex_screw_M4_10_003  label="Hex screw M4 10.003"
  LinkPlacement = pos=(39.9468,-20.0575,-20.5) rot=(0,0,1;0rad)
  LinkedObject = -> <external ../secondary/bolts.FCStd>#Body002
  Placement = pos=(39.9468,-20.0575,-20.5) rot=(0,0,1;0rad)
FEATURE [App::FeaturePython] Joint005  label="Fixed005"  # Assembly joint (typed FeaturePython)
  Activated = true
  AngleMax = 0
  AngleMin = 0
  Detach1 = false
  Detach2 = false
  Distance = 0
  Distance2 = 0
  EnableAngleMax = false
  EnableAngleMin = false
  EnableLengthMax = false
  EnableLengthMin = false
  JointType = 0 (Fixed)
  LengthMax = 0
  LengthMin = 0
  Placement1 = pos=(-6.98683,35.5575,10) rot=(0,0,1;0rad)
  Placement2 = pos=(32.96,-15.5,10.5) rot=(0,0,1;0rad)
  Reference1 = -> Assembly [Hex_screw_M4_10_003.Edge3,Hex_screw_M4_10_003.Edge3]
  Reference2 = -> Assembly [cam_holder_base.Edge93,cam_holder_base.Edge93]
FEATURE [App::FeaturePython] Joint006  label="Fixed006"  # Assembly joint (typed FeaturePython)
  Activated = true
  AngleMax = 0
  AngleMin = 0
  Detach1 = false
  Detach2 = false
  Distance = 0
  Distance2 = 0
  EnableAngleMax = false
  EnableAngleMin = false
  EnableLengthMax = false
  EnableLengthMin = false
  JointType = 0 (Fixed)
  LengthMax = 0
  LengthMin = 0
  Placement1 = pos=(-6.98683,35.5575,10) rot=(0,0,1;0rad)
  Placement2 = pos=(32.96,22.5,10.5) rot=(0,0,1;0rad)
  Reference1 = -> Assembly [Hex_screw_M4_10_002.Edge3,Hex_screw_M4_10_002.Edge3]
  Reference2 = -> Assembly [cam_holder_base.Edge89,cam_holder_base.Edge89]
FEATURE [App::FeaturePython] Joint007  label="Fixed007"  # Assembly joint (typed FeaturePython)
  Activated = true
  AngleMax = 0
  AngleMin = 0
  Detach1 = false
  Detach2 = false
  Distance = 0
  Distance2 = 0
  EnableAngleMax = false
  EnableAngleMin = false
  EnableLengthMax = false
  EnableLengthMin = false
  JointType = 0 (Fixed)
  LengthMax = 0
  LengthMin = 0
  Placement1 = pos=(-6.98683,35.5575,10) rot=(0,0,1;0rad)
  Placement2 = pos=(-32.96,-15.5,10.5) rot=(0,0,1;0rad)
  Reference1 = -> Assembly [Hex_screw_M4_10_001.Edge3,Hex_screw_M4_10_001.Edge3]
  Reference2 = -> Assembly [cam_holder_base.Edge74,cam_holder_base.Edge74]
FEATURE [App::FeaturePython] Joint008  label="Fixed008"  # Assembly joint (typed FeaturePython)
  Activated = true
  AngleMax = 0
  AngleMin = 0
  Detach1 = false
  Detach2 = false
  Distance = 0
  Distance2 = 0
  EnableAngleMax = false
  EnableAngleMin = false
  EnableLengthMax = false
  EnableLengthMin = false
  JointType = 0 (Fixed)
  LengthMax = 0
  LengthMin = 0
  Placement1 = pos=(-6.98683,35.5575,10) rot=(0,0,1;0rad)
  Placement2 = pos=(-32.96,22.5,10.5) rot=(0,0,1;0rad)
  Reference1 = -> Assembly [Hex_screw_M4_10_0.Edge3,Hex_screw_M4_10_0.Edge3]
  Reference2 = -> Assembly [cam_holder_base.Edge85,cam_holder_base.Edge85]
FEATURE [Assembly::JointGroup] Joints
  Group = -> [GroundedJoint,Joint,Joint001,Joint002,Joint003,Joint004,Joint005,Joint006,Joint007,Joint008]
FEATURE [Assembly::AssemblyObject] Assembly  label="asm_cam_mount"
  Group = -> [Joints,cam_holder_base,GroundedJoint,Raspberry_Pi_HQ_Camera_with_cs_mount_lens_v014,Joint,Hex_screw_M2_5_04_0,Hex_screw_M2_5_04_001,Hex_screw_M2_5_04_002,Hex_screw_M2_5_04_003,Joint001,Joint002,Joint003,Joint004,Hex_screw_M4_10_0,Hex_screw_M4_10_001,Hex_screw_M4_10_002,Hex_screw_M4_10_003,Joint005,Joint006,Joint007,Joint008]
  Origin = -> Origin
  Type = Assembly
---- part asm_rpi.FCStd = doc fcstd_5018777385bd ----
FCSTD DOCUMENT  (FreeCAD 1.0R39109 (Git))
Label: asm_rpi
License: All rights reserved
LicenseURL: https://en.wikipedia.org/wiki/All_rights_reserved
objects: App::Link×5, App::FeaturePython×5, Assembly::JointGroup×1, Assembly::AssemblyObject×1
EXTERNAL_REF file=../downloads/raspberry_pi_4_model_b.FCStd obj=Raspberry_Pi_4_Model_B
EXTERNAL_REF file=../secondary/bolts.FCStd obj=Body003

FEATURE [App::Link] Raspberry_Pi_4_Model_B  label="Raspberry Pi 4 Model B"
  LinkPlacement = pos=(0,8.25,-5.85) rot=(1,0,0;1.5708rad)
  LinkedObject = -> <external ../downloads/raspberry_pi_4_model_b.FCStd>#Raspberry_Pi_4_Model_B
  Placement = pos=(0,8.25,-5.85) rot=(1,0,0;1.5708rad)
FEATURE [App::FeaturePython] GroundedJoint  # Assembly grounded joint (typed FeaturePython)
  ObjectToGround = -> Raspberry_Pi_4_Model_B
  Placement = pos=(0,8.25,-5.85) rot=(1,0,0;1.5708rad)
FEATURE [App::Link] Hex_screw_M2_5_04_0  label="Hex screw M2.5 04.0"
  LinkPlacement = pos=(54.5575,25.7632,-2.56) rot=(-0.707107,0.707107,0;3.14159rad)
  LinkedObject = -> <external ../secondary/bolts.FCStd>#Body003
  Placement = pos=(54.5575,25.7632,-2.56) rot=(-0.707107,0.707107,0;3.14159rad)
FEATURE [App::Link] Hex_screw_M2_5_04_001  label="Hex screw M2.5 04.001"
  LinkPlacement = pos=(-3.44249,-23.2368,-2.56001) rot=(-0.707107,0.707107,0;3.14159rad)
  LinkedObject = -> <external ../secondary/bolts.FCStd>#Body003
  Placement = pos=(-3.44249,-23.2368,-2.56001) rot=(-0.707107,0.707107,0;3.14159rad)
FEATURE [App::Link] Hex_screw_M2_5_04_002  label="Hex screw M2.5 04.002"
  LinkPlacement = pos=(-3.44249,25.7632,-2.56) rot=(-0.707107,0.707107,0;3.14159rad)
  LinkedObject = -> <external ../secondary/bolts.FCStd>#Body003
  Placement = pos=(-3.44249,25.7632,-2.56) rot=(-0.707107,0.707107,0;3.14159rad)
FEATURE [App::Link] Hex_screw_M2_5_04_003  label="Hex screw M2.5 04.003"
  LinkPlacement = pos=(54.5575,-23.2368,-2.56001) rot=(-0.707107,0.707107,0;3.14159rad)
  LinkedObject = -> <external ../secondary/bolts.FCStd>#Body003
  Placement = pos=(54.5575,-23.2368,-2.56001) rot=(-0.707107,0.707107,0;3.14159rad)
FEATURE [App::FeaturePython] Joint  label="Fixed"  # Assembly joint (typed FeaturePython)
  Activated = true
  AngleMax = 0
  AngleMin = 0
  Detach1 = false
  Detach2 = false
  Distance = 0
  Distance2 = 0
  EnableAngleMax = false
  EnableAngleMin = false
  EnableLengthMax = false
  EnableLengthMin = false
  JointType = 0 (Fixed)
  LengthMax = 0
  LengthMin = 0
  Placement1 = pos=(-6.98683,35.5575,2.5) rot=(0,0,1;0rad)
  Placement2 = pos=(-39,0.79,-24.5) rot=(0.57735,0.57735,0.57735;4.18879rad)
  Reference1 = -> Assembly [Hex_screw_M2_5_04_002.Edge4,Hex_screw_M2_5_04_002.Edge4]
  Reference2 = -> Assembly [Raspberry_Pi_4_Model_B.Part__Feature.Edge62,Raspberry_Pi_4_Model_B.Part__Feature.Edge62]
FEATURE [App::FeaturePython] Joint001  label="Fixed001"  # Assembly joint (typed FeaturePython)
  Activated = true
  AngleMax = 0
  AngleMin = 0
  Detach1 = false
  Detach2 = false
  Distance = 0
  Distance2 = 0
  EnableAngleMax = false
  EnableAngleMin = false
  EnableLengthMax = false
  EnableLengthMin = false
  JointType = 0 (Fixed)
  LengthMax = 0
  LengthMin = 0
  Placement1 = pos=(-6.98683,35.5575,2.5) rot=(0,0,1;0rad)
  Placement2 = pos=(19,0.79,-24.5) rot=(0.57735,0.57735,0.57735;4.18879rad)
  Reference1 = -> Assembly [Hex_screw_M2_5_04_0.Edge4,Hex_screw_M2_5_04_0.Edge4]
  Reference2 = -> Assembly [Raspberry_Pi_4_Model_B.Part__Feature.Edge70,Raspberry_Pi_4_Model_B.Part__Feature.Edge70]
FEATURE [App::FeaturePython] Joint002  label="Fixed002"  # Assembly joint (typed FeaturePython)
  Activated = true
  AngleMax = 0
  AngleMin = 0
  Detach1 = false
  Detach2 = false
  Distance = 0
  Distance2 = 0
  EnableAngleMax = false
  EnableAngleMin = false
  EnableLengthMax = false
  EnableLengthMin = false
  JointType = 0 (Fixed)
  LengthMax = 0
  LengthMin = 0
  Placement1 = pos=(-6.98683,35.5575,2.5) rot=(0,0,1;0rad)
  Placement2 = pos=(19,0.79,24.5) rot=(0.57735,0.57735,0.57735;4.18879rad)
  Reference1 = -> Assembly [Hex_screw_M2_5_04_003.Edge4,Hex_screw_M2_5_04_003.Edge4]
  Reference2 = -> Assembly [Raspberry_Pi_4_Model_B.Part__Feature.Edge336,Raspberry_Pi_4_Model_B.Part__Feature.Edge336]
FEATURE [App::FeaturePython] Joint003  label="Fixed003"  # Assembly joint (typed FeaturePython)
  Activated = true
  AngleMax = 0
  AngleMin = 0
  Detach1 = false
  Detach2 = false
  Distance = 0
  Distance2 = 0
  EnableAngleMax = false
  EnableAngleMin = false
  EnableLengthMax = false
  EnableLengthMin = false
  JointType = 0 (Fixed)
  LengthMax = 0
  LengthMin = 0
  Placement1 = pos=(-6.98683,35.5575,2.5) rot=(0,0,1;0rad)
  Placement2 = pos=(-39,0.79,24.5) rot=(0.57735,0.57735,0.57735;4.18879rad)
  Reference1 = -> Assembly [Hex_screw_M2_5_04_001.Edge4,Hex_screw_M2_5_04_001.Edge4]
  Reference2 = -> Assembly [Raspberry_Pi_4_Model_B.Part__Feature.Edge340,Raspberry_Pi_4_Model_B.Part__Feature.Edge340]
FEATURE [Assembly::JointGroup] Joints
  Group = -> [GroundedJoint,Joint,Joint001,Joint002,Joint003]
FEATURE [Assembly::AssemblyObject] Assembly  label="asm_rpi"
  Group = -> [Joints,Raspberry_Pi_4_Model_B,GroundedJoint,Hex_screw_M2_5_04_0,Hex_screw_M2_5_04_001,Hex_screw_M2_5_04_002,Hex_screw_M2_5_04_003,Joint,Joint001,Joint002,Joint003]
  Origin = -> Origin
  Type = Assembly
---- part asm_shf.FCStd = doc fcstd_04160f494026 ----
FCSTD DOCUMENT  (FreeCAD 1.0R39109 (Git))
Label: asm_shf
License: All rights reserved
LicenseURL: https://en.wikipedia.org/wiki/All_rights_reserved
objects: App::Link×4, App::FeaturePython×3, Assembly::JointGroup×1, Assembly::AssemblyObject×1
EXTERNAL_REF file=../downloads/linear-bearing-shaft-support-shf12-1.snapshot.1/SHF_12.FCStd obj=Part__Feature
EXTERNAL_REF file=../secondary/bolts.FCStd obj=BOLTS_part001
EXTERNAL_REF file=../secondary/bolts.FCStd obj=BOLTS_part004

FEATURE [App::Link] SHF12
  LinkedObject = -> <external ../downloads/linear-bearing-shaft-support-shf12-1.snapshot.1/SHF_12.FCStd>#Part__Feature
FEATURE [App::FeaturePython] GroundedJoint  # Assembly grounded joint (typed FeaturePython)
  ObjectToGround = -> SHF12
FEATURE [App::Link] Hex_socket_head_cap_screw_DIN_912_M4_15_0  label="Hex socket head cap screw DIN 912 M4 15.0"
  LinkPlacement = pos=(12.25,6.5,11.5) rot=(0,-1,0;1.5708rad)
  LinkedObject = -> <external ../secondary/bolts.FCStd>#BOLTS_part001
  Placement = pos=(12.25,6.5,11.5) rot=(0,-1,0;1.5708rad)
FEATURE [App::Link] Hex_socket_head_cap_screw_DIN_912_M5_15_0  label="Hex socket head cap screw DIN 912 M5 15.0"
  LinkPlacement = pos=(18,11,1.16e-14) rot=(0.57735,-0.57735,0.57735;2.0944rad)
  LinkedObject = -> <external ../secondary/bolts.FCStd>#BOLTS_part004
  Placement = pos=(18,11,1.16e-14) rot=(0.57735,-0.57735,0.57735;2.0944rad)
FEATURE [App::Link] Hex_socket_head_cap_screw_DIN_912_M5_15_001  label="Hex socket head cap screw DIN 912 M5 15.001"
  LinkPlacement = pos=(-18,11,1.16e-14) rot=(0.57735,-0.57735,0.57735;2.0944rad)
  LinkedObject = -> <external ../secondary/bolts.FCStd>#BOLTS_part004
  Placement = pos=(-18,11,1.16e-14) rot=(0.57735,-0.57735,0.57735;2.0944rad)
FEATURE [App::FeaturePython] Joint001  label="Fixed001"  # Assembly joint (typed FeaturePython)
  Activated = true
  AngleMax = 0
  AngleMin = 0
  Detach1 = false
  Detach2 = false
  Distance = 0
  Distance2 = 0
  EnableAngleMax = false
  EnableAngleMin = false
  EnableLengthMax = false
  EnableLengthMin = false
  JointType = 0 (Fixed)
  LengthMax = 0
  LengthMin = 0
  Placement1 = pos=(-18,6,1.16e-14) rot=(0.57735,0.57735,0.57735;4.18879rad)
  Placement2 = pos=(-6e-16,-3.6e-15,5) rot=(0,0,1;0rad)
  Reference1 = -> Assembly [SHF12.Edge68,SHF12.Edge68]
  Reference2 = -> Assembly [Hex_socket_head_cap_screw_DIN_912_M5_15_001.Edge4,Hex_socket_head_cap_screw_DIN_912_M5_15_001.Edge4]
FEATURE [App::FeaturePython] Joint002  label="Fixed002"  # Assembly joint (typed FeaturePython)
  Activated = true
  AngleMax = 0
  AngleMin = 0
  Detach1 = false
  Detach2 = false
  Distance = 0
  Distance2 = 0
  EnableAngleMax = false
  EnableAngleMin = false
  EnableLengthMax = false
  EnableLengthMin = false
  JointType = 0 (Fixed)
  LengthMax = 0
  LengthMin = 0
FEATURE [Assembly::JointGroup] Joints
  Group = -> [GroundedJoint,Joint001,Joint002]
FEATURE [Assembly::AssemblyObject] Assembly  label="asm_SHF"
  Group = -> [Joints,SHF12,GroundedJoint,Hex_socket_head_cap_screw_DIN_912_M4_15_0,Hex_socket_head_cap_screw_DIN_912_M5_15_0,Hex_socket_head_cap_screw_DIN_912_M5_15_001,Joint001,Joint002]
  Origin = -> Origin
  Type = Assembly
